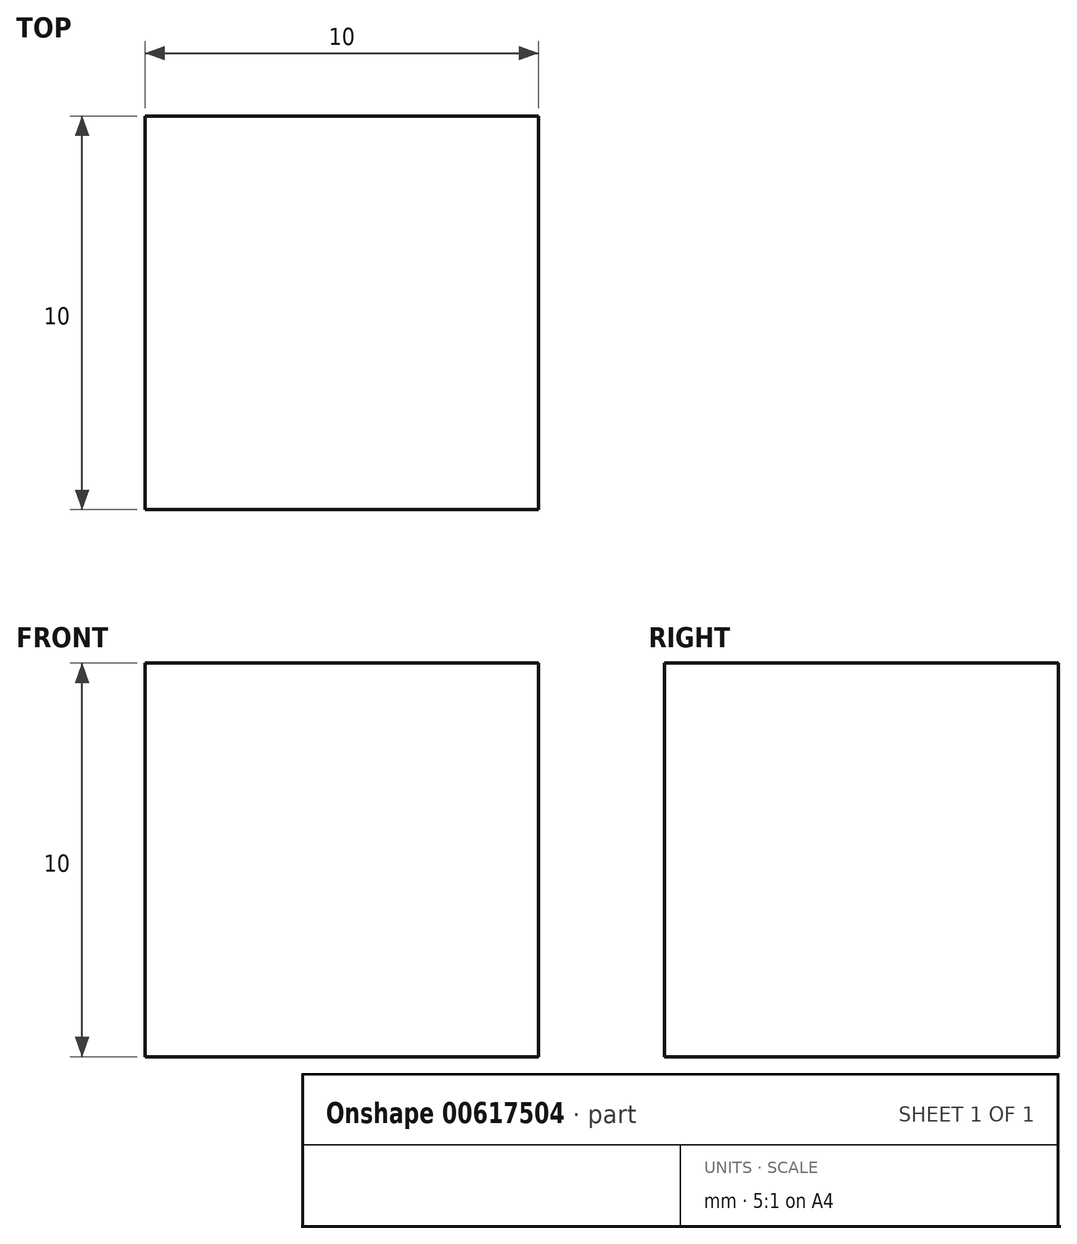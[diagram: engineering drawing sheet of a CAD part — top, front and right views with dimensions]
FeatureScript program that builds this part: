
annotation { "Feature Type Name" : "Feature", "Feature Type Description" : "" }
export const myFeature = defineFeature(function(context is Context, id is Id, definition is map)
    precondition{}
    {
        {
            var Q0;
            Q0=qCreatedBy(makeId("Top.planeOp"),FACE);
            var sketch = newSketch(context, id + "F0", { "sketchPlane" : qUnion([Q0])});
            skLineSegment(sketch, "E0.bottom", {"start": v(0, 0) * mm, "end": v(10, 0) * mm});
            skLineSegment(sketch, "E0.top", {"start": v(0, 10) * mm, "end": v(10, 10) * mm});
            skLineSegment(sketch, "E0.left", {"start": v(0, 0) * mm, "end": v(0, 10) * mm});
            skLineSegment(sketch, "E0.right", {"start": v(10, 0) * mm, "end": v(10, 10) * mm});
            skSolve(sketch);
        }
        {
            var Q0;
            Q0=makeQuery(id+"F0.imprint","IMPRINT",FACE,{"disambiguationData":[TD([[makeQuery(id+"F0.imprint","IMPRINT",EDGE,{"derivedFrom":sQuery(id+"F0.wireOp",EDGE,"E0.bottom")}),1.0]])]});
            extrude(context, id + "F1", {"entities" : qUnion([Q0]), "depth" : 10 * mm, "offsetDistance" : 25 * mm});
        }
    });
